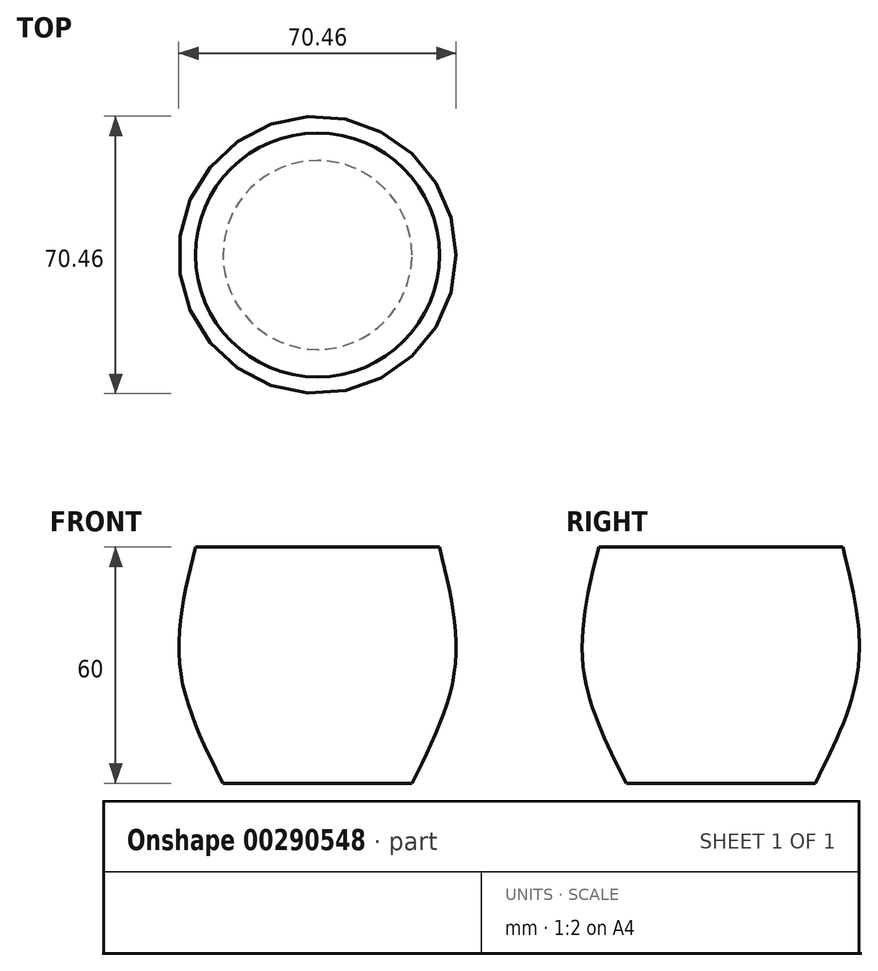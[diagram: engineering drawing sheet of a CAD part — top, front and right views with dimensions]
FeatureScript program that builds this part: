
annotation { "Feature Type Name" : "Feature", "Feature Type Description" : "" }
export const myFeature = defineFeature(function(context is Context, id is Id, definition is map)
    precondition{}
    {
        {
            var Q0;
            Q0=qCreatedBy(makeId("Top.planeOp"),FACE);
            var sketch = newSketch(context, id + "F0", { "sketchPlane" : qUnion([Q0])});
            skCircle(sketch, "E0", {"center": v(0, 0) * mm, "radius": 24 * mm});
            skSolve(sketch);
        }
        {
            var Q0;
            Q0=qCreatedBy(makeId("Top.planeOp"),FACE);
            cPlane(context, id + "F1", {"entities" : qUnion([Q0]), "cplaneType" : CPlaneType.OFFSET, "offset" : 60 * mm, "width" : 150 * mm, "height" : 150 * mm});
        }
        {
            var Q0;
            Q0=qCreatedBy(id+"F1.planeOp",FACE);
            var sketch = newSketch(context, id + "F2", { "sketchPlane" : qUnion([Q0])});
            skCircle(sketch, "E1", {"center": v(0, 0) * mm, "radius": 31 * mm});
            skSolve(sketch);
        }
        {
            var Q0;
            Q0=qCreatedBy(id+"F1.planeOp",FACE);
            cPlane(context, id + "F3", {"entities" : qUnion([Q0]), "cplaneType" : CPlaneType.OFFSET, "offset" : 30 * mm, "oppositeDirection" : true, "width" : 150 * mm, "height" : 150 * mm});
        }
        {
            var Q0;
            Q0=qCreatedBy(id+"F3.planeOp",FACE);
            var sketch = newSketch(context, id + "F4", { "sketchPlane" : qUnion([Q0])});
            skCircle(sketch, "E2", {"center": v(0, 0) * mm, "radius": 35 * mm});
            skSolve(sketch);
        }
        {
            var Q0;
            Q0 = qSketchRegion(id + "F0", true);
            var Q1;
            Q1 = qSketchRegion(id + "F4", true);
            var Q2;
            Q2 = qSketchRegion(id + "F2", true);
            loft(context, id + "F5", {"sheetProfilesArray" : [{ "sheetProfileEntities" : qUnion([Q0]) }, { "sheetProfileEntities" : qUnion([Q1]) }, { "sheetProfileEntities" : qUnion([Q2]) }]});
        }
    });
